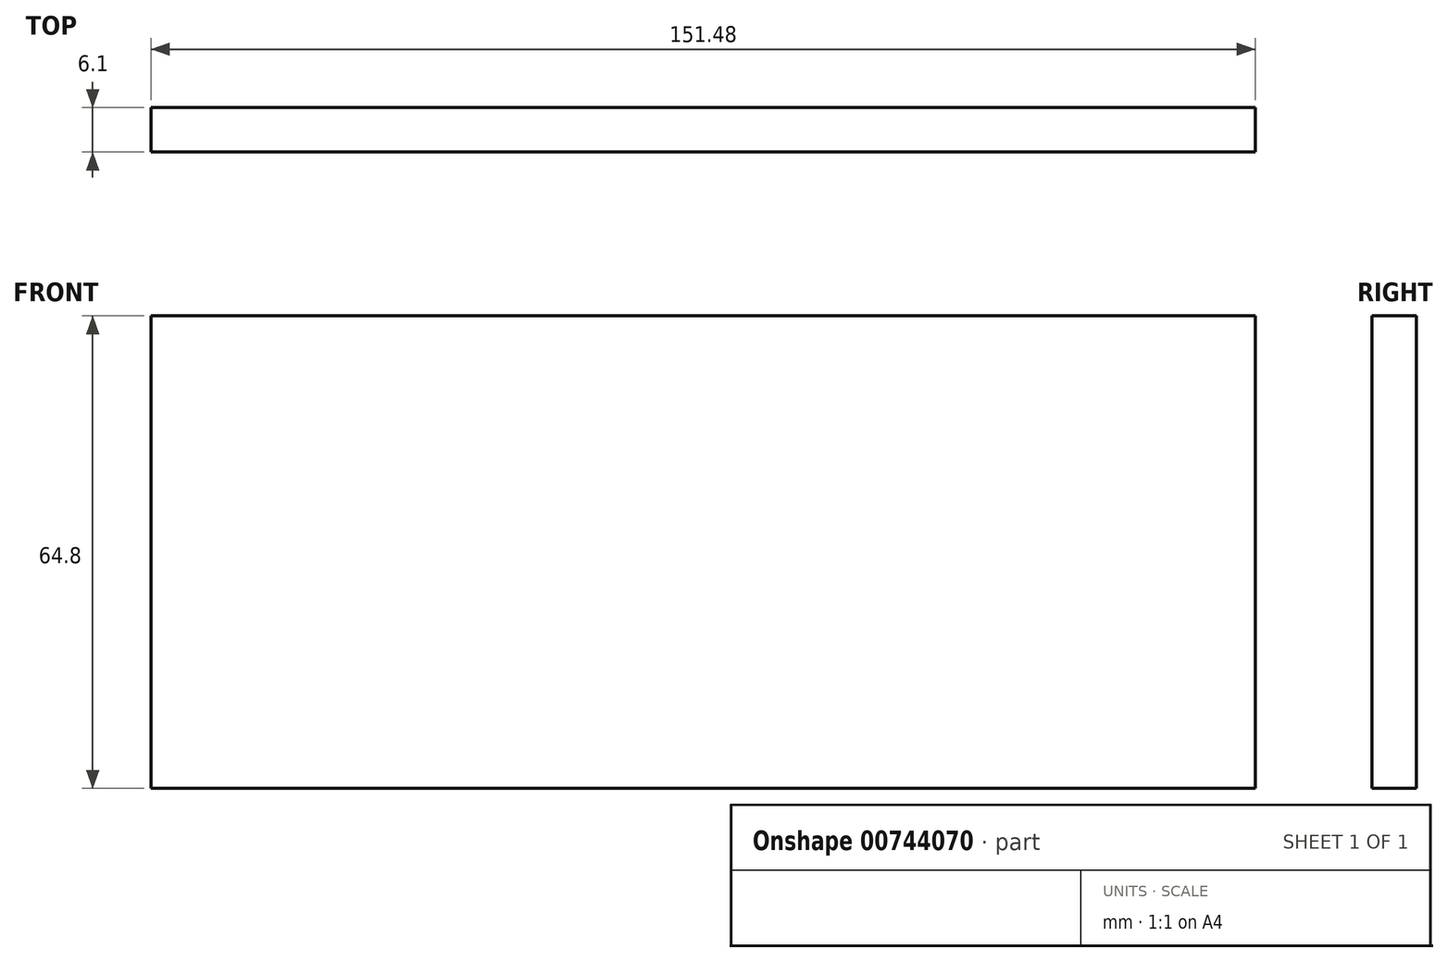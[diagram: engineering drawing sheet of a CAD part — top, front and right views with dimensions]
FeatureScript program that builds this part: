
annotation { "Feature Type Name" : "Feature", "Feature Type Description" : "" }
export const myFeature = defineFeature(function(context is Context, id is Id, definition is map)
    precondition{}
    {
        {
            var Q0;
            Q0=qCreatedBy(makeId("Front.planeOp"),FACE);
            var sketch = newSketch(context, id + "F0", { "sketchPlane" : qUnion([Q0])});
            skLineSegment(sketch, "E0.bottom", {"start": v(75.74, 32.4) * mm, "end": v(-75.74, 32.4) * mm});
            skLineSegment(sketch, "E0.top", {"start": v(75.74, -32.4) * mm, "end": v(-75.74, -32.4) * mm});
            skLineSegment(sketch, "E0.left", {"start": v(75.74, 32.4) * mm, "end": v(75.74, -32.4) * mm});
            skLineSegment(sketch, "E0.right", {"start": v(-75.74, 32.4) * mm, "end": v(-75.74, -32.4) * mm});
            skPoint(sketch, "E0.middle", {"position": v(0, 0) * mm});
            skSolve(sketch);
        }
        {
            var Q0;
            Q0=makeQuery(id+"F0.imprint","IMPRINT",FACE,{"disambiguationData":[TD([[makeQuery(id+"F0.imprint","IMPRINT",EDGE,{"derivedFrom":sQuery(id+"F0.wireOp",EDGE,"E0.bottom")}),1.0]])]});
            extrude(context, id + "F1", {"entities" : qUnion([Q0]), "depth" : 6.1 * mm, "offsetDistance" : 25.4 * mm});
        }
    });
